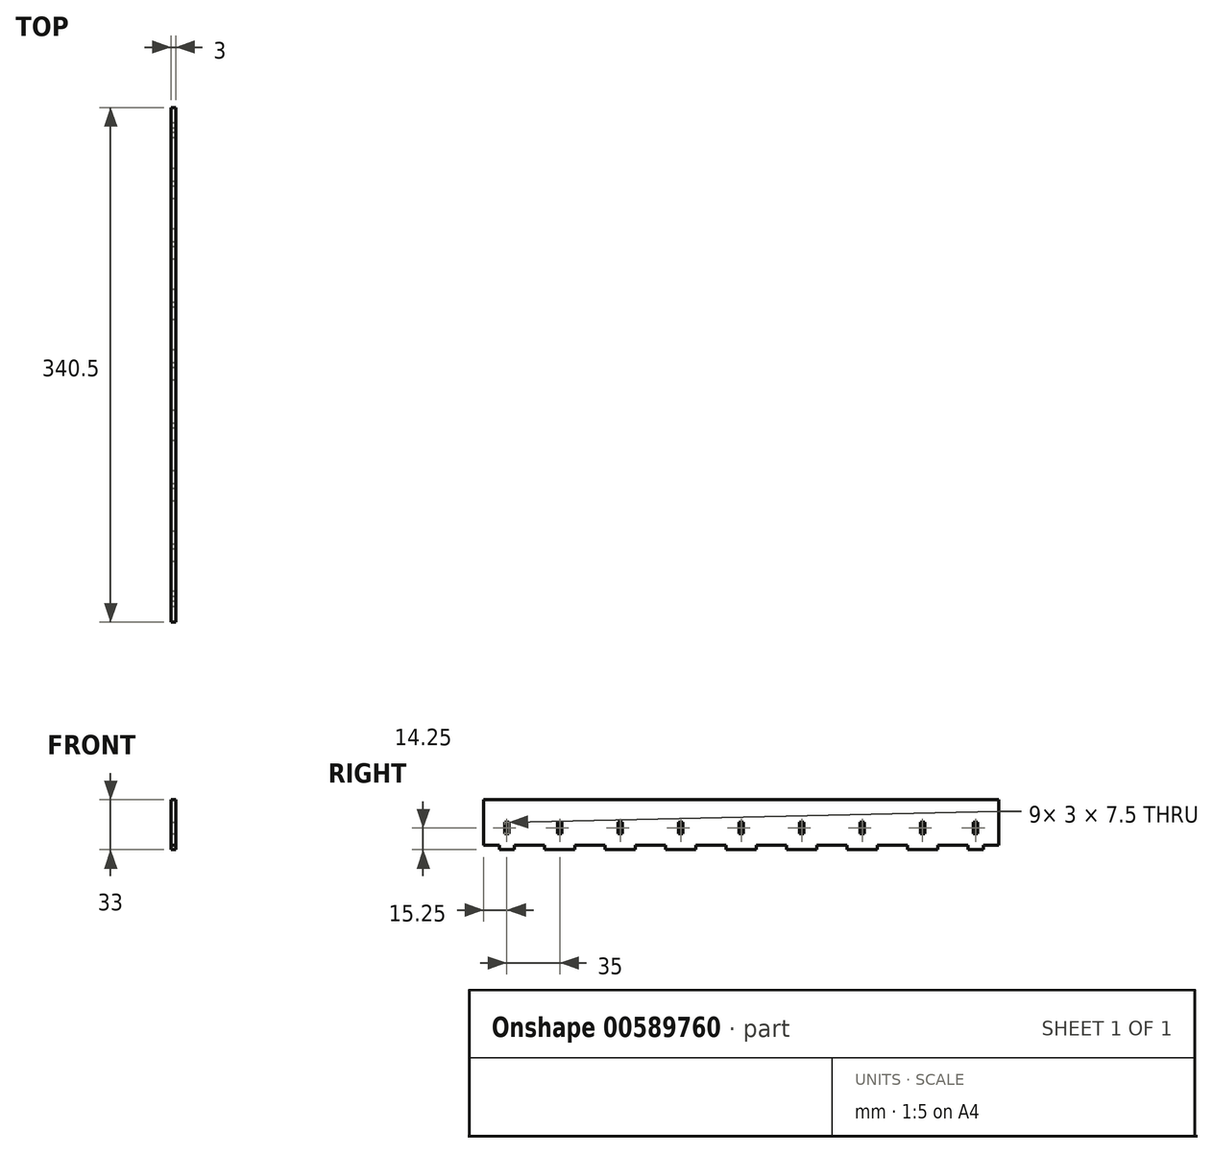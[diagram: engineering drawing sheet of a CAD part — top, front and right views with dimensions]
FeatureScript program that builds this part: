
annotation { "Feature Type Name" : "Feature", "Feature Type Description" : "" }
export const myFeature = defineFeature(function(context is Context, id is Id, definition is map)
    precondition{}
    {
        {
            var Q0;
            Q0=qCreatedBy(makeId("Right.planeOp"),FACE);
            var sketch = newSketch(context, id + "F0", { "sketchPlane" : qUnion([Q0])});
            skLineSegment(sketch, "E0.bottom", {"start": v(140, -15) * mm, "end": v(-140, -15) * mm});
            skLineSegment(sketch, "E0.top", {"start": v(140, 15) * mm, "end": v(-140, 15) * mm});
            skLineSegment(sketch, "E0.left", {"start": v(140, -15) * mm, "end": v(140, 15) * mm});
            skLineSegment(sketch, "E0.right", {"start": v(-140, -15) * mm, "end": v(-140, 15) * mm});
            skPoint(sketch, "E0.middle", {"position": v(0, 0) * mm});
            skSolve(sketch);
        }
        {
            var Q0;
            Q0=qSketchRegion(id+"F0",true);
            extrude(context, id + "F1", {"entities" : qUnion([Q0]), "depth" : 3 * mm, "offsetDistance" : 25 * mm});
        }
        {
            var Q0;
            Q0=makeQuery(id+"F1.opExtrude","CAP_FACE",FACE,{"disambiguationData":[OSD([sQuery(id+"F0.wireOp",EDGE,"E0.bottom"),sQuery(id+"F0.wireOp",EDGE,"E0.top"),sQuery(id+"F0.wireOp",EDGE,"E0.left"),sQuery(id+"F0.wireOp",EDGE,"E0.right")])],"isStart":false});
            var sketch = newSketch(context, id + "F2", { "sketchPlane" : qUnion([Q0])});
            skLineSegment(sketch, "E1", {"start": v(140, -15) * mm, "end": v(130, -15) * mm, "construction": true});
            skLineSegment(sketch, "E2.bottom", {"start": v(130, -15) * mm, "end": v(110, -15) * mm});
            skLineSegment(sketch, "E2.top", {"start": v(130, -18) * mm, "end": v(110, -18) * mm});
            skLineSegment(sketch, "E2.left", {"start": v(130, -15) * mm, "end": v(130, -18) * mm});
            skLineSegment(sketch, "E2.right", {"start": v(110, -15) * mm, "end": v(110, -18) * mm});
            skLineSegment(sketch, "E3.1.0.0", {"start": v(90, -15) * mm, "end": v(90, -18) * mm});
            skLineSegment(sketch, "E3.1.0.1", {"start": v(90, -15) * mm, "end": v(70, -15) * mm});
            skLineSegment(sketch, "E3.1.0.2", {"start": v(90, -18) * mm, "end": v(70, -18) * mm});
            skLineSegment(sketch, "E3.1.0.3", {"start": v(70, -15) * mm, "end": v(70, -18) * mm});
            skLineSegment(sketch, "E3.2.0.0", {"start": v(50, -15) * mm, "end": v(50, -18) * mm});
            skLineSegment(sketch, "E3.2.0.1", {"start": v(50, -15) * mm, "end": v(30, -15) * mm});
            skLineSegment(sketch, "E3.2.0.2", {"start": v(50, -18) * mm, "end": v(30, -18) * mm});
            skLineSegment(sketch, "E3.2.0.3", {"start": v(30, -15) * mm, "end": v(30, -18) * mm});
            skLineSegment(sketch, "E3.3.0.0", {"start": v(10, -15) * mm, "end": v(10, -18) * mm});
            skLineSegment(sketch, "E3.3.0.1", {"start": v(10, -15) * mm, "end": v(-10, -15) * mm});
            skLineSegment(sketch, "E3.3.0.2", {"start": v(10, -18) * mm, "end": v(-10, -18) * mm});
            skLineSegment(sketch, "E3.3.0.3", {"start": v(-10, -15) * mm, "end": v(-10, -18) * mm});
            skLineSegment(sketch, "E3.4.0.0", {"start": v(-30, -15) * mm, "end": v(-30, -18) * mm});
            skLineSegment(sketch, "E3.4.0.1", {"start": v(-30, -15) * mm, "end": v(-50, -15) * mm});
            skLineSegment(sketch, "E3.4.0.2", {"start": v(-30, -18) * mm, "end": v(-50, -18) * mm});
            skLineSegment(sketch, "E3.4.0.3", {"start": v(-50, -15) * mm, "end": v(-50, -18) * mm});
            skLineSegment(sketch, "E3.5.0.0", {"start": v(-70, -15) * mm, "end": v(-70, -18) * mm});
            skLineSegment(sketch, "E3.5.0.1", {"start": v(-70, -15) * mm, "end": v(-90, -15) * mm});
            skLineSegment(sketch, "E3.5.0.2", {"start": v(-70, -18) * mm, "end": v(-90, -18) * mm});
            skLineSegment(sketch, "E3.5.0.3", {"start": v(-90, -15) * mm, "end": v(-90, -18) * mm});
            skLineSegment(sketch, "E3.6.0.0", {"start": v(-110, -15) * mm, "end": v(-110, -18) * mm});
            skLineSegment(sketch, "E3.6.0.1", {"start": v(-110, -15) * mm, "end": v(-130, -15) * mm});
            skLineSegment(sketch, "E3.6.0.2", {"start": v(-110, -18) * mm, "end": v(-130, -18) * mm});
            skLineSegment(sketch, "E3.6.0.3", {"start": v(-130, -15) * mm, "end": v(-130, -18) * mm});
            skLineSegment(sketch, "E3.direction1", {"start": v(130, -18) * mm, "end": v(90, -18) * mm, "construction": true});
            skSolve(sketch);
        }
        {
            var Q0;
            Q0=qSketchRegion(id+"F2",true);
            var Q1;
            Q1=makeQuery(id+"F1.opExtrude","CAP_FACE",FACE,{"disambiguationData":[OSD([sQuery(id+"F0.wireOp",EDGE,"E0.bottom"),sQuery(id+"F0.wireOp",EDGE,"E0.top"),sQuery(id+"F0.wireOp",EDGE,"E0.left"),sQuery(id+"F0.wireOp",EDGE,"E0.right")])],"isStart":true});
            extrude(context, id + "F3", {"entities" : qUnion([Q0]), "operationType" : NewBodyOperationType.ADD, "endBound" : BoundingType.UP_TO_SURFACE, "oppositeDirection" : true, "depth" : 25 * mm, "endBoundEntityFace" : qUnion([Q1]), "offsetDistance" : 25 * mm});
        }
        {
            var Q0;
            Q0=makeQuery(id+"F3.boolean.opBoolean","MERGE",FACE,{"derivedFrom":[makeQuery(id+"F1.opExtrude","CAP_FACE",FACE,{"disambiguationData":[OSD([sQuery(id+"F0.wireOp",EDGE,"E0.bottom"),sQuery(id+"F0.wireOp",EDGE,"E0.top"),sQuery(id+"F0.wireOp",EDGE,"E0.left"),sQuery(id+"F0.wireOp",EDGE,"E0.right")])],"isStart":false}),makeQuery(id+"F3.opExtrude","CAP_FACE",FACE,{"disambiguationData":[OSD([sQuery(id+"F2.wireOp",EDGE,"E2.bottom"),sQuery(id+"F2.wireOp",EDGE,"E2.top"),sQuery(id+"F2.wireOp",EDGE,"E2.left"),sQuery(id+"F2.wireOp",EDGE,"E2.right")])],"isStart":true}),makeQuery(id+"F3.opExtrude","CAP_FACE",FACE,{"disambiguationData":[OSD([sQuery(id+"F2.wireOp",EDGE,"E3.1.0.0"),sQuery(id+"F2.wireOp",EDGE,"E3.1.0.1"),sQuery(id+"F2.wireOp",EDGE,"E3.1.0.2"),sQuery(id+"F2.wireOp",EDGE,"E3.1.0.3")])],"isStart":true}),makeQuery(id+"F3.opExtrude","CAP_FACE",FACE,{"disambiguationData":[OSD([sQuery(id+"F2.wireOp",EDGE,"E3.2.0.0"),sQuery(id+"F2.wireOp",EDGE,"E3.2.0.1"),sQuery(id+"F2.wireOp",EDGE,"E3.2.0.2"),sQuery(id+"F2.wireOp",EDGE,"E3.2.0.3")])],"isStart":true}),makeQuery(id+"F3.opExtrude","CAP_FACE",FACE,{"disambiguationData":[OSD([sQuery(id+"F2.wireOp",EDGE,"E3.3.0.0"),sQuery(id+"F2.wireOp",EDGE,"E3.3.0.1"),sQuery(id+"F2.wireOp",EDGE,"E3.3.0.2"),sQuery(id+"F2.wireOp",EDGE,"E3.3.0.3")])],"isStart":true}),makeQuery(id+"F3.opExtrude","CAP_FACE",FACE,{"disambiguationData":[OSD([sQuery(id+"F2.wireOp",EDGE,"E3.4.0.0"),sQuery(id+"F2.wireOp",EDGE,"E3.4.0.1"),sQuery(id+"F2.wireOp",EDGE,"E3.4.0.2"),sQuery(id+"F2.wireOp",EDGE,"E3.4.0.3")])],"isStart":true}),makeQuery(id+"F3.opExtrude","CAP_FACE",FACE,{"disambiguationData":[OSD([sQuery(id+"F2.wireOp",EDGE,"E3.5.0.0"),sQuery(id+"F2.wireOp",EDGE,"E3.5.0.1"),sQuery(id+"F2.wireOp",EDGE,"E3.5.0.2"),sQuery(id+"F2.wireOp",EDGE,"E3.5.0.3")])],"isStart":true}),makeQuery(id+"F3.opExtrude","CAP_FACE",FACE,{"disambiguationData":[OSD([sQuery(id+"F2.wireOp",EDGE,"E3.6.0.0"),sQuery(id+"F2.wireOp",EDGE,"E3.6.0.1"),sQuery(id+"F2.wireOp",EDGE,"E3.6.0.2"),sQuery(id+"F2.wireOp",EDGE,"E3.6.0.3")])],"isStart":true})]});
            var sketch = newSketch(context, id + "F4", { "sketchPlane" : qUnion([Q0])});
            skLineSegment(sketch, "E4", {"start": v(130, -15) * mm, "end": v(110, -15) * mm, "construction": true});
            skLineSegment(sketch, "E5", {"start": v(120, -15) * mm, "end": v(120, -3.75) * mm, "construction": true});
            skLineSegment(sketch, "E6.bottom", {"start": v(121.5, -7.5) * mm, "end": v(118.5, -7.5) * mm});
            skLineSegment(sketch, "E6.top", {"start": v(121.5, 0) * mm, "end": v(118.5, 0) * mm});
            skLineSegment(sketch, "E6.left", {"start": v(121.5, -7.5) * mm, "end": v(121.5, 0) * mm});
            skLineSegment(sketch, "E6.right", {"start": v(118.5, -7.5) * mm, "end": v(118.5, 0) * mm});
            skPoint(sketch, "E6.middle", {"position": v(120, -3.75) * mm});
            skLineSegment(sketch, "E7.1.0.0", {"start": v(81.5, -7.5) * mm, "end": v(81.5, 0) * mm});
            skLineSegment(sketch, "E7.1.0.1", {"start": v(81.5, 0) * mm, "end": v(78.5, 0) * mm});
            skLineSegment(sketch, "E7.1.0.2", {"start": v(78.5, -7.5) * mm, "end": v(78.5, 0) * mm});
            skLineSegment(sketch, "E7.1.0.3", {"start": v(81.5, -7.5) * mm, "end": v(78.5, -7.5) * mm});
            skLineSegment(sketch, "E7.2.0.0", {"start": v(41.5, -7.5) * mm, "end": v(41.5, 0) * mm});
            skLineSegment(sketch, "E7.2.0.1", {"start": v(41.5, 0) * mm, "end": v(38.5, 0) * mm});
            skLineSegment(sketch, "E7.2.0.2", {"start": v(38.5, -7.5) * mm, "end": v(38.5, 0) * mm});
            skLineSegment(sketch, "E7.2.0.3", {"start": v(41.5, -7.5) * mm, "end": v(38.5, -7.5) * mm});
            skLineSegment(sketch, "E7.3.0.0", {"start": v(1.5, -7.5) * mm, "end": v(1.5, 0) * mm});
            skLineSegment(sketch, "E7.3.0.1", {"start": v(1.5, 0) * mm, "end": v(-1.5, 0) * mm});
            skLineSegment(sketch, "E7.3.0.2", {"start": v(-1.5, -7.5) * mm, "end": v(-1.5, 0) * mm});
            skLineSegment(sketch, "E7.3.0.3", {"start": v(1.5, -7.5) * mm, "end": v(-1.5, -7.5) * mm});
            skLineSegment(sketch, "E7.4.0.0", {"start": v(-38.5, -7.5) * mm, "end": v(-38.5, 0) * mm});
            skLineSegment(sketch, "E7.4.0.1", {"start": v(-38.5, 0) * mm, "end": v(-41.5, 0) * mm});
            skLineSegment(sketch, "E7.4.0.2", {"start": v(-41.5, -7.5) * mm, "end": v(-41.5, 0) * mm});
            skLineSegment(sketch, "E7.4.0.3", {"start": v(-38.5, -7.5) * mm, "end": v(-41.5, -7.5) * mm});
            skLineSegment(sketch, "E7.5.0.0", {"start": v(-78.5, -7.5) * mm, "end": v(-78.5, 0) * mm});
            skLineSegment(sketch, "E7.5.0.1", {"start": v(-78.5, 0) * mm, "end": v(-81.5, 0) * mm});
            skLineSegment(sketch, "E7.5.0.2", {"start": v(-81.5, -7.5) * mm, "end": v(-81.5, 0) * mm});
            skLineSegment(sketch, "E7.5.0.3", {"start": v(-78.5, -7.5) * mm, "end": v(-81.5, -7.5) * mm});
            skLineSegment(sketch, "E7.6.0.0", {"start": v(-118.5, -7.5) * mm, "end": v(-118.5, 0) * mm});
            skLineSegment(sketch, "E7.6.0.1", {"start": v(-118.5, 0) * mm, "end": v(-121.5, 0) * mm});
            skLineSegment(sketch, "E7.6.0.2", {"start": v(-121.5, -7.5) * mm, "end": v(-121.5, 0) * mm});
            skLineSegment(sketch, "E7.6.0.3", {"start": v(-118.5, -7.5) * mm, "end": v(-121.5, -7.5) * mm});
            skLineSegment(sketch, "E7.direction1", {"start": v(121.5, -7.5) * mm, "end": v(81.5, -7.5) * mm, "construction": true});
            skSolve(sketch);
        }
        {
            var Q0;
            Q0=qSketchRegion(id+"F4",true);
            extrude(context, id + "F5", {"entities" : qUnion([Q0]), "operationType" : NewBodyOperationType.REMOVE, "oppositeDirection" : true, "depth" : 25 * mm, "offsetDistance" : 25 * mm});
        }
        {
            var Q0;
            Q0=makeQuery(id+"F3.boolean.opBoolean","MERGE",FACE,{"derivedFrom":[makeQuery(id+"F1.opExtrude","CAP_FACE",FACE,{"disambiguationData":[OSD([sQuery(id+"F0.wireOp",EDGE,"E0.bottom"),sQuery(id+"F0.wireOp",EDGE,"E0.top"),sQuery(id+"F0.wireOp",EDGE,"E0.left"),sQuery(id+"F0.wireOp",EDGE,"E0.right")])],"isStart":false}),makeQuery(id+"F3.opExtrude","CAP_FACE",FACE,{"disambiguationData":[OSD([sQuery(id+"F2.wireOp",EDGE,"E2.bottom"),sQuery(id+"F2.wireOp",EDGE,"E2.top"),sQuery(id+"F2.wireOp",EDGE,"E2.left"),sQuery(id+"F2.wireOp",EDGE,"E2.right")])],"isStart":true}),makeQuery(id+"F3.opExtrude","CAP_FACE",FACE,{"disambiguationData":[OSD([sQuery(id+"F2.wireOp",EDGE,"E3.1.0.0"),sQuery(id+"F2.wireOp",EDGE,"E3.1.0.1"),sQuery(id+"F2.wireOp",EDGE,"E3.1.0.2"),sQuery(id+"F2.wireOp",EDGE,"E3.1.0.3")])],"isStart":true}),makeQuery(id+"F3.opExtrude","CAP_FACE",FACE,{"disambiguationData":[OSD([sQuery(id+"F2.wireOp",EDGE,"E3.2.0.0"),sQuery(id+"F2.wireOp",EDGE,"E3.2.0.1"),sQuery(id+"F2.wireOp",EDGE,"E3.2.0.2"),sQuery(id+"F2.wireOp",EDGE,"E3.2.0.3")])],"isStart":true}),makeQuery(id+"F3.opExtrude","CAP_FACE",FACE,{"disambiguationData":[OSD([sQuery(id+"F2.wireOp",EDGE,"E3.3.0.0"),sQuery(id+"F2.wireOp",EDGE,"E3.3.0.1"),sQuery(id+"F2.wireOp",EDGE,"E3.3.0.2"),sQuery(id+"F2.wireOp",EDGE,"E3.3.0.3")])],"isStart":true}),makeQuery(id+"F3.opExtrude","CAP_FACE",FACE,{"disambiguationData":[OSD([sQuery(id+"F2.wireOp",EDGE,"E3.4.0.0"),sQuery(id+"F2.wireOp",EDGE,"E3.4.0.1"),sQuery(id+"F2.wireOp",EDGE,"E3.4.0.2"),sQuery(id+"F2.wireOp",EDGE,"E3.4.0.3")])],"isStart":true}),makeQuery(id+"F3.opExtrude","CAP_FACE",FACE,{"disambiguationData":[OSD([sQuery(id+"F2.wireOp",EDGE,"E3.5.0.0"),sQuery(id+"F2.wireOp",EDGE,"E3.5.0.1"),sQuery(id+"F2.wireOp",EDGE,"E3.5.0.2"),sQuery(id+"F2.wireOp",EDGE,"E3.5.0.3")])],"isStart":true}),makeQuery(id+"F3.opExtrude","CAP_FACE",FACE,{"disambiguationData":[OSD([sQuery(id+"F2.wireOp",EDGE,"E3.6.0.0"),sQuery(id+"F2.wireOp",EDGE,"E3.6.0.1"),sQuery(id+"F2.wireOp",EDGE,"E3.6.0.2"),sQuery(id+"F2.wireOp",EDGE,"E3.6.0.3")])],"isStart":true})]});
            var sketch = newSketch(context, id + "F6", { "sketchPlane" : qUnion([Q0])});
            skLineSegment(sketch, "E8.bottom", {"start": v(-140, 15) * mm, "end": v(-170.25, 15) * mm});
            skLineSegment(sketch, "E8.top", {"start": v(-140, -15) * mm, "end": v(-170.25, -15) * mm});
            skLineSegment(sketch, "E8.left", {"start": v(-140, 15) * mm, "end": v(-140, -15) * mm});
            skLineSegment(sketch, "E8.right", {"start": v(-170.25, 15) * mm, "end": v(-170.25, -15) * mm});
            skLineSegment(sketch, "E9.MirrorCS", {"start": v(140, -15) * mm, "end": v(170.25, -15) * mm});
            skLineSegment(sketch, "E10.MirrorCS", {"start": v(140, 15) * mm, "end": v(140, -15) * mm});
            skLineSegment(sketch, "E11.MirrorCS", {"start": v(170.25, 15) * mm, "end": v(170.25, -15) * mm});
            skLineSegment(sketch, "E12.MirrorCS", {"start": v(140, 15) * mm, "end": v(170.25, 15) * mm});
            skSolve(sketch);
        }
        {
            var Q0;
            Q0=makeQuery(id+"F6.imprint","IMPRINT",FACE,{"disambiguationData":[TD([[makeQuery(id+"F6.imprint","IMPRINT",EDGE,{"derivedFrom":sQuery(id+"F6.wireOp",EDGE,"E8.bottom")}),1.0]])]});
            var Q1;
            Q1=makeQuery(id+"F6.imprint","IMPRINT",FACE,{"disambiguationData":[TD([[makeQuery(id+"F6.imprint","IMPRINT",EDGE,{"derivedFrom":sQuery(id+"F6.wireOp",EDGE,"E9.MirrorCS")}),1.0]])]});
            extrude(context, id + "F7", {"entities" : qUnion([Q0, Q1]), "operationType" : NewBodyOperationType.ADD, "oppositeDirection" : true, "depth" : 3 * mm, "offsetDistance" : 25 * mm});
        }
        {
            var Q0;
            {var subQ0=sQuery(id+"F0.wireOp",EDGE,"E0.right");var subQ1=sQuery(id+"F0.wireOp",EDGE,"E0.left");var subQ2=sQuery(id+"F0.wireOp",EDGE,"E0.top");var subQ3=sQuery(id+"F0.wireOp",EDGE,"E0.bottom");Q0=makeQuery(id+"F7.boolean.opBoolean","MERGE",FACE,{"derivedFrom":[makeQuery(id+"F3.boolean.opBoolean","MERGE",FACE,{"derivedFrom":[makeQuery(id+"F1.opExtrude","CAP_FACE",FACE,{"disambiguationData":[OSD([subQ3,subQ2,subQ1,subQ0])],"isStart":true}),makeQuery(id+"F3.opExtrude","CAP_FACE",FACE,{"disambiguationData":[OSD([subQ3,subQ2,subQ1,subQ0]),OD(0.0)],"isStart":false}),makeQuery(id+"F3.opExtrude","CAP_FACE",FACE,{"disambiguationData":[OSD([subQ3,subQ2,subQ1,subQ0]),OD(1.0)],"isStart":false}),makeQuery(id+"F3.opExtrude","CAP_FACE",FACE,{"disambiguationData":[OSD([subQ3,subQ2,subQ1,subQ0]),OD(2.0)],"isStart":false}),makeQuery(id+"F3.opExtrude","CAP_FACE",FACE,{"disambiguationData":[OSD([subQ3,subQ2,subQ1,subQ0]),OD(3.0)],"isStart":false}),makeQuery(id+"F3.opExtrude","CAP_FACE",FACE,{"disambiguationData":[OSD([subQ3,subQ2,subQ1,subQ0]),OD(4.0)],"isStart":false}),makeQuery(id+"F3.opExtrude","CAP_FACE",FACE,{"disambiguationData":[OSD([subQ3,subQ2,subQ1,subQ0]),OD(5.0)],"isStart":false}),makeQuery(id+"F3.opExtrude","CAP_FACE",FACE,{"disambiguationData":[OSD([subQ3,subQ2,subQ1,subQ0]),OD(6.0)],"isStart":false})]}),makeQuery(id+"F7.opExtrude","CAP_FACE",FACE,{"disambiguationData":[OSD([sQuery(id+"F6.wireOp",EDGE,"E8.bottom"),sQuery(id+"F6.wireOp",EDGE,"E8.top"),sQuery(id+"F6.wireOp",EDGE,"E8.left"),sQuery(id+"F6.wireOp",EDGE,"E8.right")])],"isStart":false}),makeQuery(id+"F7.opExtrude","CAP_FACE",FACE,{"disambiguationData":[OSD([sQuery(id+"F6.wireOp",EDGE,"E9.MirrorCS"),sQuery(id+"F6.wireOp",EDGE,"E10.MirrorCS"),sQuery(id+"F6.wireOp",EDGE,"E11.MirrorCS"),sQuery(id+"F6.wireOp",EDGE,"E12.MirrorCS")])],"isStart":false})]});}
            var sketch = newSketch(context, id + "F8", { "sketchPlane" : qUnion([Q0])});
            skLineSegment(sketch, "E13", {"start": v(-130, -15) * mm, "end": v(-150, -15) * mm, "construction": true});
            skLineSegment(sketch, "E14.bottom", {"start": v(-150, -15) * mm, "end": v(-160, -15) * mm});
            skLineSegment(sketch, "E14.top", {"start": v(-150, -18) * mm, "end": v(-160, -18) * mm});
            skLineSegment(sketch, "E14.left", {"start": v(-150, -15) * mm, "end": v(-150, -18) * mm});
            skLineSegment(sketch, "E14.right", {"start": v(-160, -15) * mm, "end": v(-160, -18) * mm});
            skLineSegment(sketch, "E15.MirrorCS", {"start": v(160, -15) * mm, "end": v(160, -18) * mm});
            skLineSegment(sketch, "E16.MirrorCS", {"start": v(150, -15) * mm, "end": v(150, -18) * mm});
            skLineSegment(sketch, "E17.MirrorCS", {"start": v(150, -15) * mm, "end": v(160, -15) * mm});
            skLineSegment(sketch, "E18.MirrorCS", {"start": v(150, -18) * mm, "end": v(160, -18) * mm});
            skSolve(sketch);
        }
        {
            var Q0;
            Q0 = qSketchRegion(id + "F8", true);
            extrude(context, id + "F9", {"entities" : qUnion([Q0]), "operationType" : NewBodyOperationType.ADD, "oppositeDirection" : true, "depth" : 3 * mm, "offsetDistance" : 25 * mm});
        }
        {
            var Q0;
            {var subQ0=sQuery(id+"F0.wireOp",EDGE,"E0.right");var subQ1=sQuery(id+"F0.wireOp",EDGE,"E0.left");var subQ2=sQuery(id+"F0.wireOp",EDGE,"E0.top");var subQ3=sQuery(id+"F0.wireOp",EDGE,"E0.bottom");Q0=makeQuery(id+"F9.boolean.opBoolean","MERGE",FACE,{"derivedFrom":[makeQuery(id+"F7.boolean.opBoolean","MERGE",FACE,{"derivedFrom":[makeQuery(id+"F3.boolean.opBoolean","MERGE",FACE,{"derivedFrom":[makeQuery(id+"F1.opExtrude","CAP_FACE",FACE,{"disambiguationData":[OSD([subQ3,subQ2,subQ1,subQ0])],"isStart":true}),makeQuery(id+"F3.opExtrude","CAP_FACE",FACE,{"disambiguationData":[OSD([subQ3,subQ2,subQ1,subQ0]),OD(0.0)],"isStart":false}),makeQuery(id+"F3.opExtrude","CAP_FACE",FACE,{"disambiguationData":[OSD([subQ3,subQ2,subQ1,subQ0]),OD(1.0)],"isStart":false}),makeQuery(id+"F3.opExtrude","CAP_FACE",FACE,{"disambiguationData":[OSD([subQ3,subQ2,subQ1,subQ0]),OD(2.0)],"isStart":false}),makeQuery(id+"F3.opExtrude","CAP_FACE",FACE,{"disambiguationData":[OSD([subQ3,subQ2,subQ1,subQ0]),OD(3.0)],"isStart":false}),makeQuery(id+"F3.opExtrude","CAP_FACE",FACE,{"disambiguationData":[OSD([subQ3,subQ2,subQ1,subQ0]),OD(4.0)],"isStart":false}),makeQuery(id+"F3.opExtrude","CAP_FACE",FACE,{"disambiguationData":[OSD([subQ3,subQ2,subQ1,subQ0]),OD(5.0)],"isStart":false}),makeQuery(id+"F3.opExtrude","CAP_FACE",FACE,{"disambiguationData":[OSD([subQ3,subQ2,subQ1,subQ0]),OD(6.0)],"isStart":false})]}),makeQuery(id+"F7.opExtrude","CAP_FACE",FACE,{"disambiguationData":[OSD([sQuery(id+"F6.wireOp",EDGE,"E8.bottom"),sQuery(id+"F6.wireOp",EDGE,"E8.top"),sQuery(id+"F6.wireOp",EDGE,"E8.left"),sQuery(id+"F6.wireOp",EDGE,"E8.right")])],"isStart":false}),makeQuery(id+"F7.opExtrude","CAP_FACE",FACE,{"disambiguationData":[OSD([sQuery(id+"F6.wireOp",EDGE,"E9.MirrorCS"),sQuery(id+"F6.wireOp",EDGE,"E10.MirrorCS"),sQuery(id+"F6.wireOp",EDGE,"E11.MirrorCS"),sQuery(id+"F6.wireOp",EDGE,"E12.MirrorCS")])],"isStart":false})]}),makeQuery(id+"F9.opExtrude","CAP_FACE",FACE,{"disambiguationData":[OSD([sQuery(id+"F8.wireOp",EDGE,"E14.bottom"),sQuery(id+"F8.wireOp",EDGE,"E14.top"),sQuery(id+"F8.wireOp",EDGE,"E14.left"),sQuery(id+"F8.wireOp",EDGE,"E14.right")])],"isStart":true}),makeQuery(id+"F9.opExtrude","CAP_FACE",FACE,{"disambiguationData":[OSD([sQuery(id+"F8.wireOp",EDGE,"E15.MirrorCS"),sQuery(id+"F8.wireOp",EDGE,"E16.MirrorCS"),sQuery(id+"F8.wireOp",EDGE,"E17.MirrorCS"),sQuery(id+"F8.wireOp",EDGE,"E18.MirrorCS")])],"isStart":true})]});}
            var sketch = newSketch(context, id + "F10", { "sketchPlane" : qUnion([Q0])});
            skLineSegment(sketch, "E19", {"start": v(-155, -18) * mm, "end": v(-155, 15) * mm, "construction": true});
            skLineSegment(sketch, "E20", {"start": v(-121.5, -3.75) * mm, "end": v(-155, -3.75) * mm, "construction": true});
            skLineSegment(sketch, "E21.bottom", {"start": v(-153.5, 0) * mm, "end": v(-156.5, 0) * mm});
            skLineSegment(sketch, "E21.top", {"start": v(-153.5, -7.5) * mm, "end": v(-156.5, -7.5) * mm});
            skLineSegment(sketch, "E21.left", {"start": v(-153.5, 0) * mm, "end": v(-153.5, -7.5) * mm});
            skLineSegment(sketch, "E21.right", {"start": v(-156.5, 0) * mm, "end": v(-156.5, -7.5) * mm});
            skPoint(sketch, "E21.middle", {"position": v(-155, -3.75) * mm});
            skLineSegment(sketch, "E22.MirrorCS", {"start": v(156.5, 0) * mm, "end": v(156.5, -7.5) * mm});
            skLineSegment(sketch, "E23.MirrorCS", {"start": v(153.5, 0) * mm, "end": v(153.5, -7.5) * mm});
            skLineSegment(sketch, "E24.MirrorCS", {"start": v(153.5, -7.5) * mm, "end": v(156.5, -7.5) * mm});
            skLineSegment(sketch, "E25.MirrorCS", {"start": v(153.5, 0) * mm, "end": v(156.5, 0) * mm});
            skPoint(sketch, "E26.MirrorP", {"position": v(155, -3.75) * mm});
            skSolve(sketch);
        }
        {
            var Q0;
            Q0 = qSketchRegion(id + "F10", true);
            extrude(context, id + "F11", {"entities" : qUnion([Q0]), "operationType" : NewBodyOperationType.REMOVE, "oppositeDirection" : true, "depth" : 25 * mm, "offsetDistance" : 25 * mm});
        }
    });
